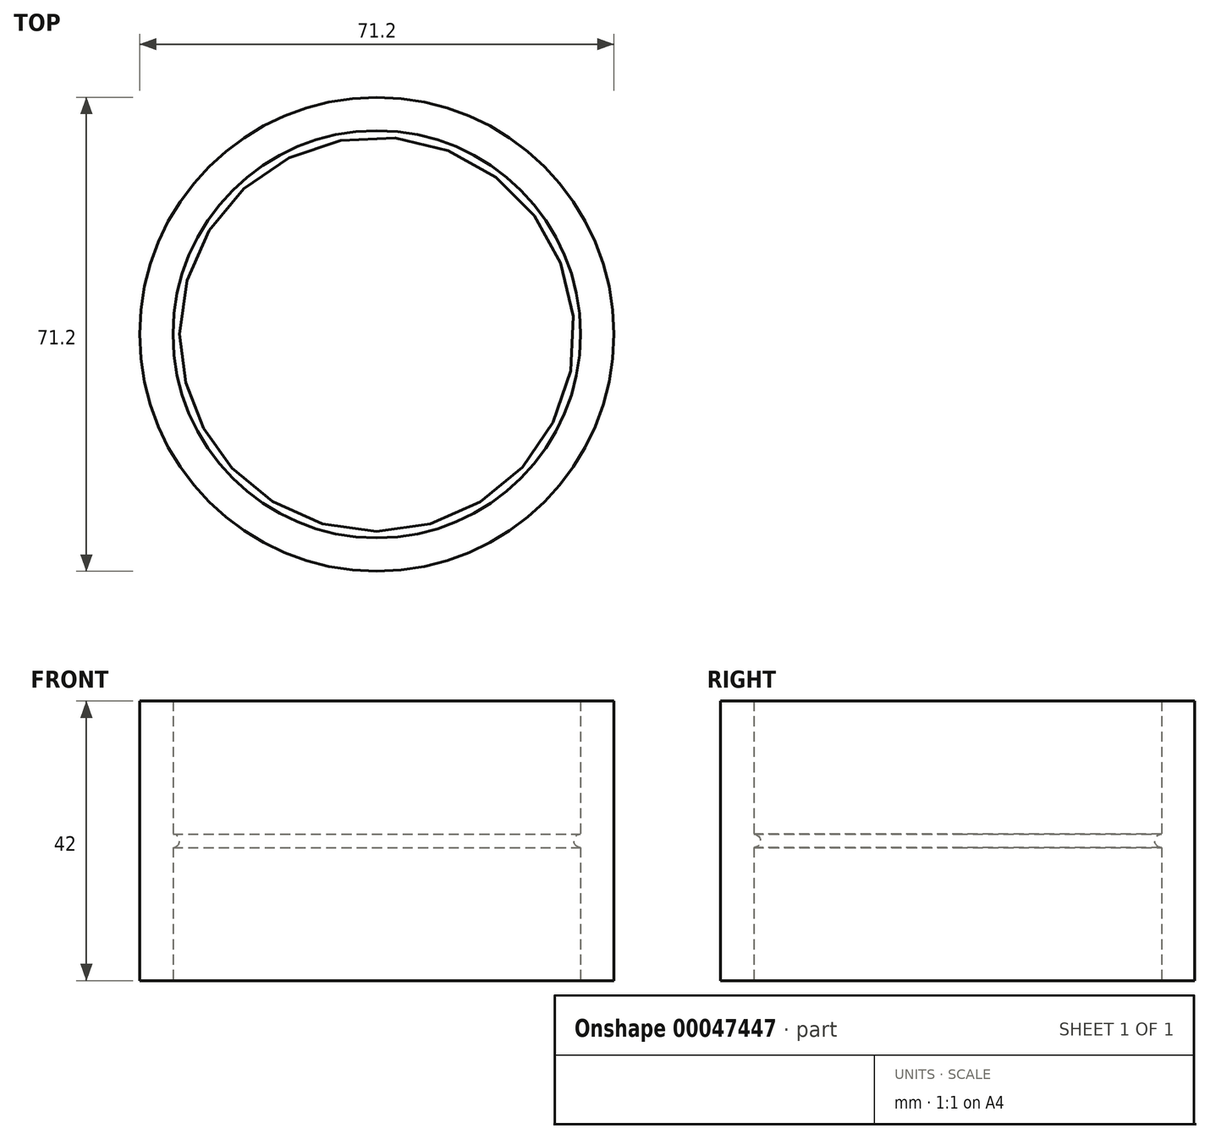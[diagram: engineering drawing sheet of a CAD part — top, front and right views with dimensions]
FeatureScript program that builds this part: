
annotation { "Feature Type Name" : "Feature", "Feature Type Description" : "" }
export const myFeature = defineFeature(function(context is Context, id is Id, definition is map)
    precondition{}
    {
        {
            var Q0;
            Q0=qCreatedBy(makeId("Front.planeOp"),FACE);
            var sketch = newSketch(context, id + "F0", { "sketchPlane" : qUnion([Q0])});
            skLineSegment(sketch, "E0", {"start": v(0, 0) * mm, "end": v(-30.6, 0) * mm, "construction": true});
            skLineSegment(sketch, "E1", {"start": v(-30.6, 0) * mm, "end": v(-30.6, 20) * mm});
            skLineSegment(sketch, "E2", {"start": v(-30.6, 20) * mm, "end": v(-35.6, 20) * mm, "construction": true});
            skLineSegment(sketch, "E3", {"start": v(-35.6, 0) * mm, "end": v(-35.6, 20) * mm});
            skLineSegment(sketch, "E4", {"start": v(0, 0) * mm, "end": v(0, 20) * mm, "construction": true});
            skLineSegment(sketch, "E5", {"start": v(-30.6, 0) * mm, "end": v(-35.6, 0) * mm});
            skArc(sketch, "E6", {"start": v(-30.6, 20) * mm, "mid": v(-29.6, 21) * mm, "end": v(-30.6, 22) * mm});
            skLineSegment(sketch, "E7", {"start": v(-30.6, 22) * mm, "end": v(-30.6, 20) * mm, "construction": true});
            skLineSegment(sketch, "E8", {"start": v(-30.6, 21) * mm, "end": v(-35.6, 21) * mm, "construction": true});
            skLineSegment(sketch, "E9.MirrorCS", {"start": v(-30.6, 42) * mm, "end": v(-30.6, 22) * mm});
            skLineSegment(sketch, "E10.MirrorCS", {"start": v(-30.6, 42) * mm, "end": v(-35.6, 42) * mm});
            skLineSegment(sketch, "E11", {"start": v(-35.6, 42) * mm, "end": v(-35.6, 20) * mm});
            skSolve(sketch);
        }
        {
            var Q0;
            Q0=qSketchRegion(id+"F0",true);
            var Q1;
            Q1=sQuery(id+"F0.wireOp",EDGE,"E4");
            revolve(context, id + "F1", {"entities" : qUnion([Q0]), "axis" : qUnion([Q1]), "revolveType" : RevolveType.FULL});
        }
    });
